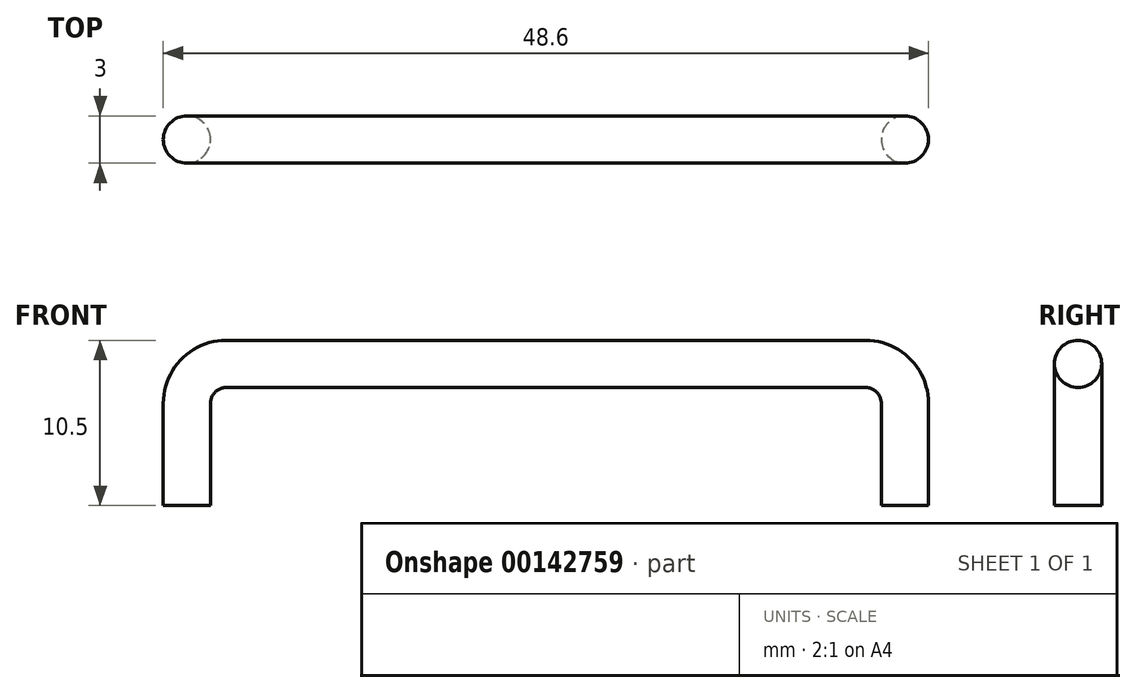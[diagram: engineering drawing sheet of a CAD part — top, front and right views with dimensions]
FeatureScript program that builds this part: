
annotation { "Feature Type Name" : "Feature", "Feature Type Description" : "" }
export const myFeature = defineFeature(function(context is Context, id is Id, definition is map)
    precondition{}
    {
        {
            var Q0;
            Q0=qCreatedBy(makeId("Front.planeOp"),FACE);
            var sketch = newSketch(context, id + "F0", { "sketchPlane" : qUnion([Q0])});
            skLineSegment(sketch, "E0", {"start": v(0, -7.5) * mm, "end": v(0, -1) * mm});
            skLineSegment(sketch, "E1", {"start": v(1, 0) * mm, "end": v(41.6, 0) * mm});
            skLineSegment(sketch, "E2", {"start": v(42.6, -1) * mm, "end": v(42.6, -7.5) * mm});
            skPoint(sketch, "E3.visualSharp", {"position": v(42.6, 0) * mm});
            skArc(sketch, "E3.filletArc", {"start": v(42.6, -1) * mm, "mid": v(42.3, -0.3) * mm, "end": v(41.6, 0) * mm});
            skPoint(sketch, "E4.visualSharp", {"position": v(0, 0) * mm});
            skArc(sketch, "E4.filletArc", {"start": v(1, 0) * mm, "mid": v(0.3, -0.3) * mm, "end": v(0, -1) * mm});
            skSolve(sketch);
        }
        {
            var Q0;
            Q0=sQuery(id+"F0.wireOp",VERTEX,"E2.end");
            var Q1;
            Q1=qCreatedBy(makeId("Top.planeOp"),FACE);
            cPlane(context, id + "F1", {"entities" : qUnion([Q0, Q1]), "cplaneType" : CPlaneType.PLANE_POINT, "offset" : 25 * mm, "width" : 150 * mm, "height" : 150 * mm});
        }
        {
            var Q0;
            Q0=qCreatedBy(id+"F1.planeOp",FACE);
            var sketch = newSketch(context, id + "F2", { "sketchPlane" : qUnion([Q0])});
            skPoint(sketch, "E5.0", {"position": v(42.6, 0) * mm});
            skCircle(sketch, "E6", {"center": v(44.1, 0) * mm, "radius": 1.5 * mm});
            skSolve(sketch);
        }
        {
            var Q0;
            Q0=makeQuery(id+"F2.imprint","IMPRINT",FACE,{"disambiguationData":[TD([[makeQuery(id+"F2.imprint","IMPRINT",EDGE,{"derivedFrom":sQuery(id+"F2.wireOp",EDGE,"E6")}),1.0]])]});
            var Q1;
            Q1=sQuery(id+"F0.wireOp",EDGE,"E2");
            var Q2;
            Q2=sQuery(id+"F0.wireOp",EDGE,"E3.filletArc");
            var Q3;
            Q3=sQuery(id+"F0.wireOp",EDGE,"E1");
            var Q4;
            Q4=sQuery(id+"F0.wireOp",EDGE,"E4.filletArc");
            var Q5;
            Q5=sQuery(id+"F0.wireOp",EDGE,"E0");
            sweep(context, id + "F3", {"profiles" : qUnion([Q0]), "path" : qUnion([Q1, Q2, Q3, Q4, Q5])});
        }
    });
